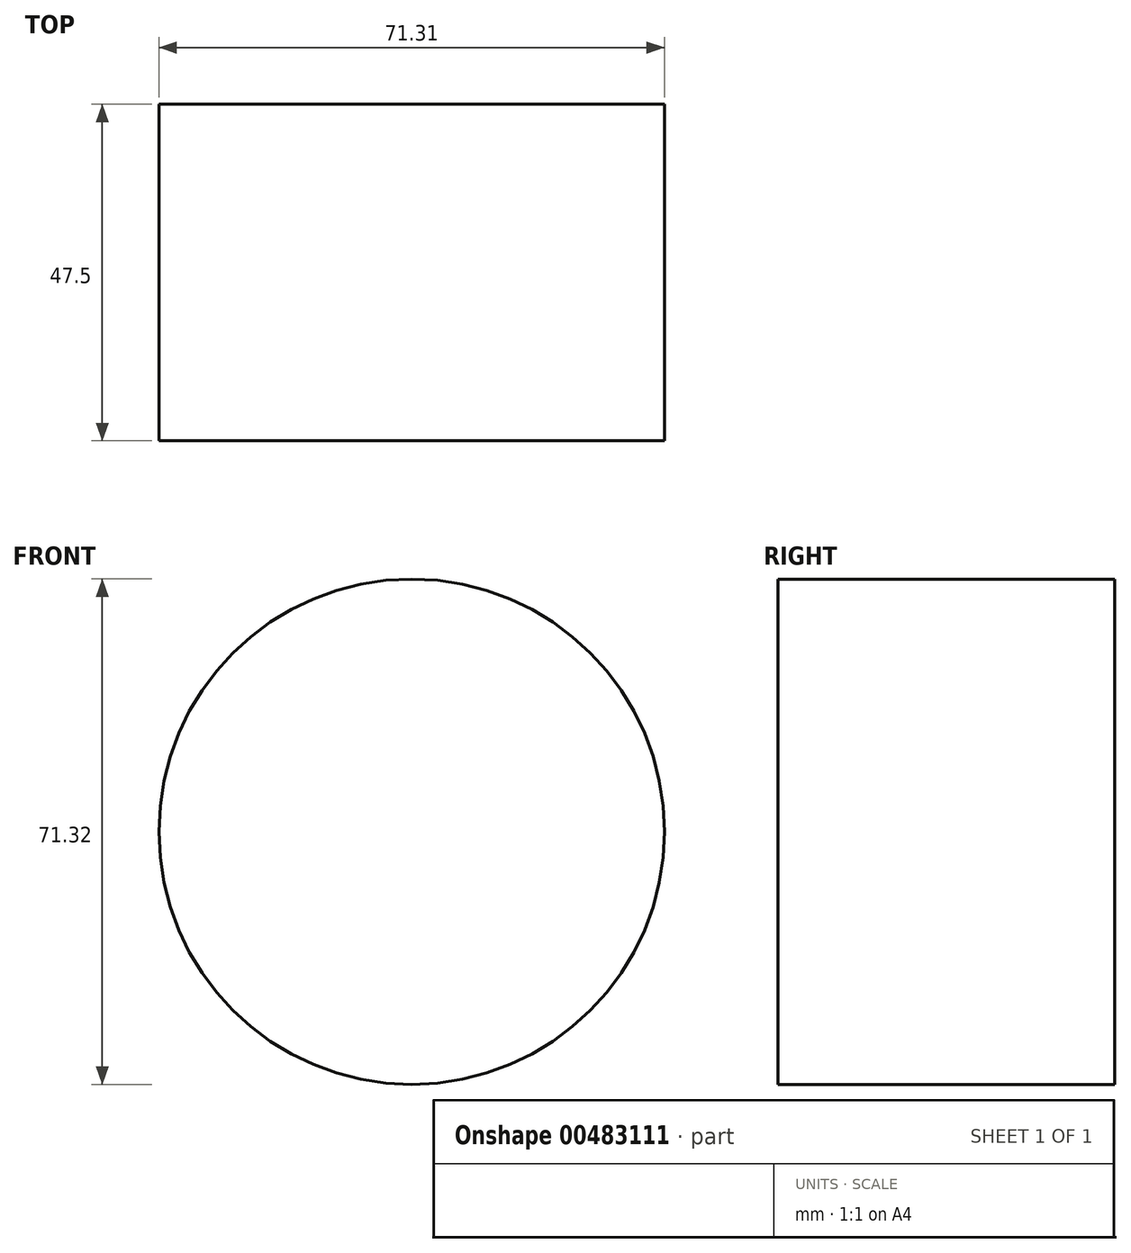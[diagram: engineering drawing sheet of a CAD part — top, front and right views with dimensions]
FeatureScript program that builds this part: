
annotation { "Feature Type Name" : "Feature", "Feature Type Description" : "" }
export const myFeature = defineFeature(function(context is Context, id is Id, definition is map)
    precondition{}
    {
        {
            var Q0;
            Q0=qCreatedBy(makeId("Front.planeOp"),FACE);
            var sketch = newSketch(context, id + "F0", { "sketchPlane" : qUnion([Q0])});
            skCircle(sketch, "E0", {"center": v(-50.4, 0) * mm, "radius": 23.62 * mm});
            skCircle(sketch, "E1", {"center": v(-50.4, 0) * mm, "radius": 35.66 * mm});
            skSolve(sketch);
        }
        {
            var Q0;
            Q0 = qSketchRegion(id + "F0", true);
            var Q1;
            Q1=makeQuery(id+"F0.imprint","IMPRINT",FACE,{"disambiguationData":[TD([[makeQuery(id+"F0.imprint","IMPRINT",EDGE,{"derivedFrom":sQuery(id+"F0.wireOp",EDGE,"E0")}),1.0]])]});
            extrude(context, id + "F1", {"entities" : qUnion([Q0, Q1]), "depth" : 22.5 * mm});
        }
        {
            var Q0;
            Q0=makeQuery(id+"F1.opExtrude","CAP_FACE",FACE,{"disambiguationData":[OSD([sQuery(id+"F0.wireOp",EDGE,"E1")])],"isStart":true});
            extrude(context, id + "F2", {"entities" : qUnion([Q0]), "operationType" : NewBodyOperationType.ADD, "depth" : 25 * mm});
        }
    });
